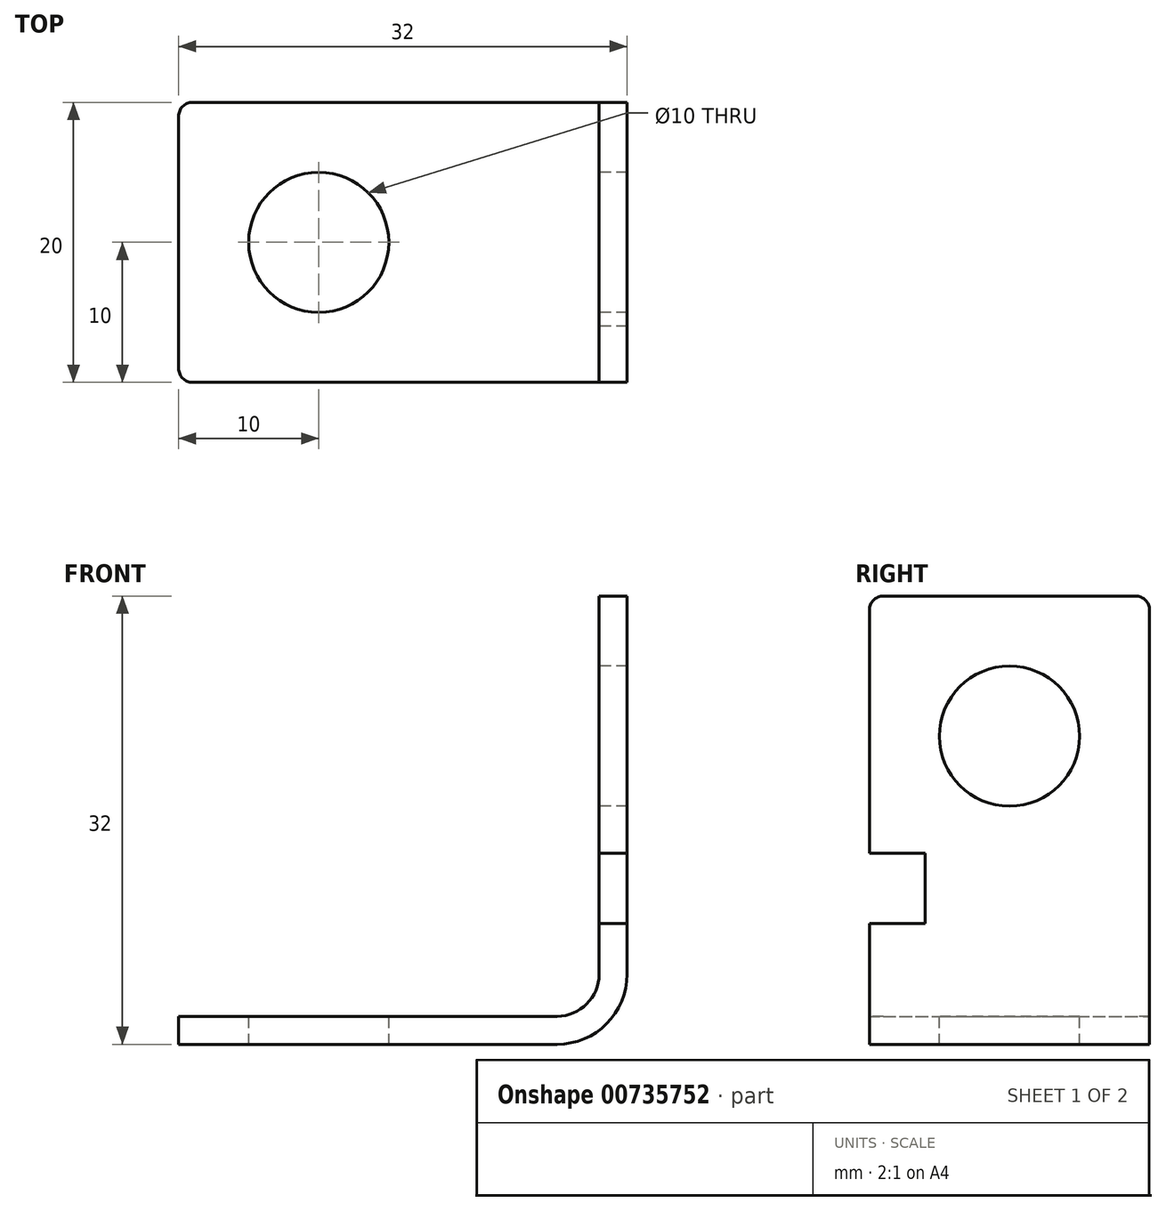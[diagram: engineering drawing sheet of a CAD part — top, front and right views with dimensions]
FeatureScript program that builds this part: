
annotation { "Feature Type Name" : "Feature", "Feature Type Description" : "" }
export const myFeature = defineFeature(function(context is Context, id is Id, definition is map)
    precondition{}
    {
        {
            var Q0;
            Q0=qCreatedBy(makeId("Front.planeOp"),FACE);
            var sketch = newSketch(context, id + "F0", { "sketchPlane" : qUnion([Q0])});
            skLineSegment(sketch, "E0", {"start": v(0, 0) * mm, "end": v(27, 0) * mm});
            skLineSegment(sketch, "E1", {"start": v(30, 3) * mm, "end": v(30, 30) * mm});
            skPoint(sketch, "E2.visualSharp", {"position": v(30, 0) * mm});
            skArc(sketch, "E2.filletArc", {"start": v(27, 0) * mm, "mid": v(29.12, 0.88) * mm, "end": v(30, 3) * mm});
            skLineSegment(sketch, "E3.0", {"start": v(32, 3) * mm, "end": v(32, 30) * mm});
            skArc(sketch, "E3.1", {"start": v(27, -2) * mm, "mid": v(30.54, -0.54) * mm, "end": v(32, 3) * mm});
            skLineSegment(sketch, "E3.2", {"start": v(0, -2) * mm, "end": v(27, -2) * mm});
            skLineSegment(sketch, "E4", {"start": v(30, 30) * mm, "end": v(32, 30) * mm});
            skLineSegment(sketch, "E5", {"start": v(0, 0) * mm, "end": v(0, -2) * mm});
            skSolve(sketch);
        }
        {
            var Q0;
            Q0 = qSketchRegion(id + "F0", true);
            extrude(context, id + "F1", {"entities" : qUnion([Q0]), "endBound" : BoundingType.SYMMETRIC, "depth" : 20 * mm, "offsetDistance" : 25.4 * mm});
        }
        {
            var Q0;
            Q0=makeQuery(id+"F1.opExtrude","SWEPT_FACE",FACE,{"disambiguationData":[OSD([sQuery(id+"F0.wireOp",EDGE,"E1")])]});
            var sketch = newSketch(context, id + "F2", { "sketchPlane" : qUnion([Q0])});
            skCircle(sketch, "E6", {"center": v(0, 20) * mm, "radius": 5 * mm});
            skSolve(sketch);
        }
        {
            var Q0;
            Q0 = qSketchRegion(id + "F2", true);
            extrude(context, id + "F3", {"entities" : qUnion([Q0]), "operationType" : NewBodyOperationType.REMOVE, "endBound" : BoundingType.UP_TO_NEXT, "oppositeDirection" : true, "depth" : 25.4 * mm, "offsetDistance" : 25.4 * mm});
        }
        {
            var Q0;
            Q0=makeQuery(id+"F1.opExtrude","SWEPT_FACE",FACE,{"disambiguationData":[OSD([sQuery(id+"F0.wireOp",EDGE,"E1")])]});
            var sketch = newSketch(context, id + "F4", { "sketchPlane" : qUnion([Q0])});
            skLineSegment(sketch, "E7.bottom", {"start": v(10, 6.63) * mm, "end": v(6, 6.63) * mm});
            skLineSegment(sketch, "E7.top", {"start": v(10, 11.63) * mm, "end": v(6, 11.63) * mm});
            skLineSegment(sketch, "E7.left", {"start": v(10, 6.63) * mm, "end": v(10, 11.63) * mm});
            skLineSegment(sketch, "E7.right", {"start": v(6, 6.63) * mm, "end": v(6, 11.63) * mm});
            skSolve(sketch);
        }
        {
            var Q0;
            Q0=makeQuery(id+"F4.imprint","IMPRINT",FACE,{"disambiguationData":[TD([[makeQuery(id+"F4.imprint","IMPRINT",EDGE,{"derivedFrom":sQuery(id+"F4.wireOp",EDGE,"E7.bottom")}),-1.0]])]});
            extrude(context, id + "F5", {"entities" : qUnion([Q0]), "operationType" : NewBodyOperationType.REMOVE, "endBound" : BoundingType.UP_TO_NEXT, "oppositeDirection" : true, "depth" : 25.4 * mm, "offsetDistance" : 25.4 * mm});
        }
        {
            var Q0;
            Q0=makeQuery(id+"F1.opExtrude","SWEPT_FACE",FACE,{"disambiguationData":[OSD([sQuery(id+"F0.wireOp",EDGE,"E0")])]});
            var sketch = newSketch(context, id + "F6", { "sketchPlane" : qUnion([Q0])});
            skCircle(sketch, "E8", {"center": v(10, 0) * mm, "radius": 5 * mm});
            skSolve(sketch);
        }
        {
            var Q0;
            Q0 = qSketchRegion(id + "F6", true);
            extrude(context, id + "F7", {"entities" : qUnion([Q0]), "operationType" : NewBodyOperationType.REMOVE, "endBound" : BoundingType.UP_TO_NEXT, "oppositeDirection" : true, "depth" : 25.4 * mm, "offsetDistance" : 25.4 * mm});
        }
        {
            var Q0;
            Q0=makeQuery(id+"F1.opExtrude","CAP_EDGE",EDGE,{"disambiguationData":[OSD([sQuery(id+"F0.wireOp",EDGE,"E4")])],"isStart":true});
            var Q1;
            Q1=makeQuery(id+"F1.opExtrude","CAP_EDGE",EDGE,{"disambiguationData":[OSD([sQuery(id+"F0.wireOp",EDGE,"E4")])],"isStart":false});
            var Q2;
            Q2=makeQuery(id+"F1.opExtrude","CAP_EDGE",EDGE,{"disambiguationData":[OSD([sQuery(id+"F0.wireOp",EDGE,"E5")])],"isStart":true});
            var Q3;
            Q3=makeQuery(id+"F1.opExtrude","CAP_EDGE",EDGE,{"disambiguationData":[OSD([sQuery(id+"F0.wireOp",EDGE,"E5")])],"isStart":false});
            fillet(context, id + "F8", {"entities" : qUnion([Q0, Q1, Q2, Q3]), "radius" : 1 * mm, "tangentPropagation" : true, "allowEdgeOverflow" : false});
        }
    });
